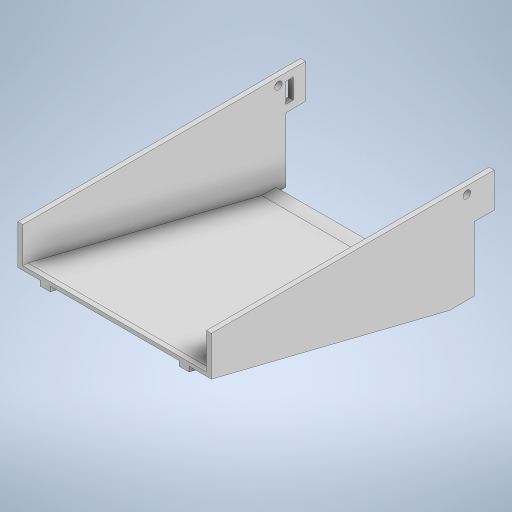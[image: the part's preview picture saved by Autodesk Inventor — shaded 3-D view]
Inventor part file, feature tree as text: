
AUTODESK INVENTOR PART (.ipt)
format: ipt  version: 2023.1 (Build 271208000, 208)  size: 330,752 bytes
history: native  units: mm
features: sketch x10, extrude x8, mirror x2, shell x1, sweep x1
ambient origin geometry x8: Origin, YZ Plane, XZ Plane, XY Plane, X Axis, Y Axis, Z Axis, Center Point
bodies: 实体1 (feature_tree)
feature tree (22):
  extrude  "拉伸1"  Depth=200.0mm
  extrude  "拉伸2"  Depth=120.0mm
  shell  "抽壳1"  Thickness=480.0mm
  extrude  "拉伸3"  Depth=10.0mm
  extrude  "拉伸4"  TaperAngle=0.0deg  [1 undecoded]
  extrude  "拉伸6"  Depth=15.0mm
  sweep  "扫掠1"
  extrude  "拉伸11"  Depth=40.0mm
  extrude  "拉伸12"  TaperAngle=0.0deg  [1 undecoded]
  mirror  "镜像3"
  mirror  "镜像4"
  extrude  "拉伸5"  TaperAngle=0.0deg  [1 undecoded]
  sketch  "草图1"  dims[d0=390.0mm d1=200.0mm]
  sketch  "草图2"  dims[d2=530.0mm d3=0.0mm d4=120.0mm d5=480.0mm]
  sketch  "草图3"  dims[d6=0.0mm d7=0.0mm d8=10.0mm]
  sketch  "草图4"  dims[d9=20.0mm d11=0.0mm d12=0.0mm]
  sketch  "草图5"  dims[d13=15.0mm d14=15.0mm]
  sketch  "草图6"  dims[d15=15.0mm d16=10.0mm d17=0.0mm]
  sketch  "草图10"  dims[d18=15.0mm d19=40.0mm]
  sketch  "草图11"  dims[d21=0.0mm d22=0.0mm d23=0.0mm]
  sketch  "草图14"  dims[d24=75.0mm d25=0.0mm d26=0.0mm]
  sketch  "草图15"  dims[d28=10.0mm d46=20.0mm d47=45.0mm d50=10.0mm d51=0.0mm d52=0.0mm d54=40.0mm d55=20.0mm d56=0.0mm d57=70.0mm d58=40.0mm d59=0.0mm d60=15.0mm]
note: 3 required parameter values undecoded (feature->parameter linkage not recoverable at this tier; creation-order binding heuristic only, values carry confidence <= 0.55)
